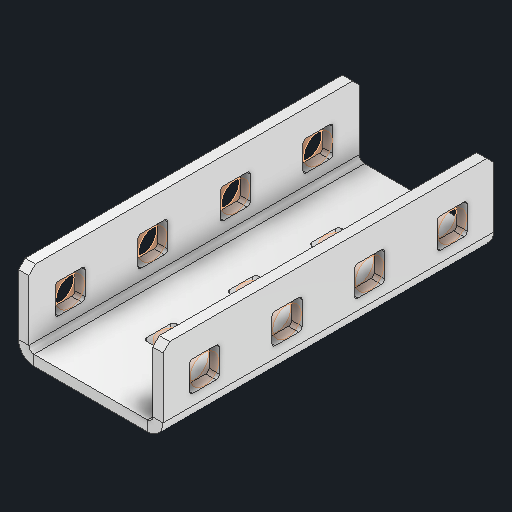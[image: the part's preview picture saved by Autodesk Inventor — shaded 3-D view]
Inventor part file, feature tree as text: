
AUTODESK INVENTOR PART (.ipt)
format: ipt  version: 2025 (Build 290162000, 162)  size: 348,672 bytes
history: native  units: in
note: dims shown in document units (in); Inventor stores cm internally (conversion verified against a paired STEP export)
features: other x27, sketch x3
ambient origin geometry x8: Origin, YZ Plane, XZ Plane, XY Plane, X Axis, Y Axis, Z Axis, Center Point
bodies: Solid1 (feature_tree)
feature tree (30):
  other  "C Channel Coupler.ipt"
  other  "Solid1::C Channel Coupler.ipt"
  other  "TaggingFeature1"
  sketch  "Sketch1"  dims[d0=0.3937in]
  sketch  "Sketch2"  dims[d1=0.0625in]
  sketch  "Sketch3"
  other  "Flange Pattern Sketch"
  other  "Flange Pattern Plane"
  other  "Srf1"
  other  "Srf2"
  other  "Srf3"
  other  "Srf4"
  other  "Srf5"
  other  "Srf6"
  other  "Srf7"
  other  "Srf8"
  other  "Srf9"
  other  "Srf10"
  other  "Srf11"
  other  "Srf1::Derived"
  other  "Srf2::Derived"
  other  "Srf823::Derived"
  other  "Srf824::Derived"
  other  "Srf825::Derived"
  other  "Srf826::Derived"
  other  "Srf827::Derived"
  other  "Srf828::Derived"
  other  "Srf786::Derived"
  other  "Srf889::Derived"
  other  "Srf890::Derived"
